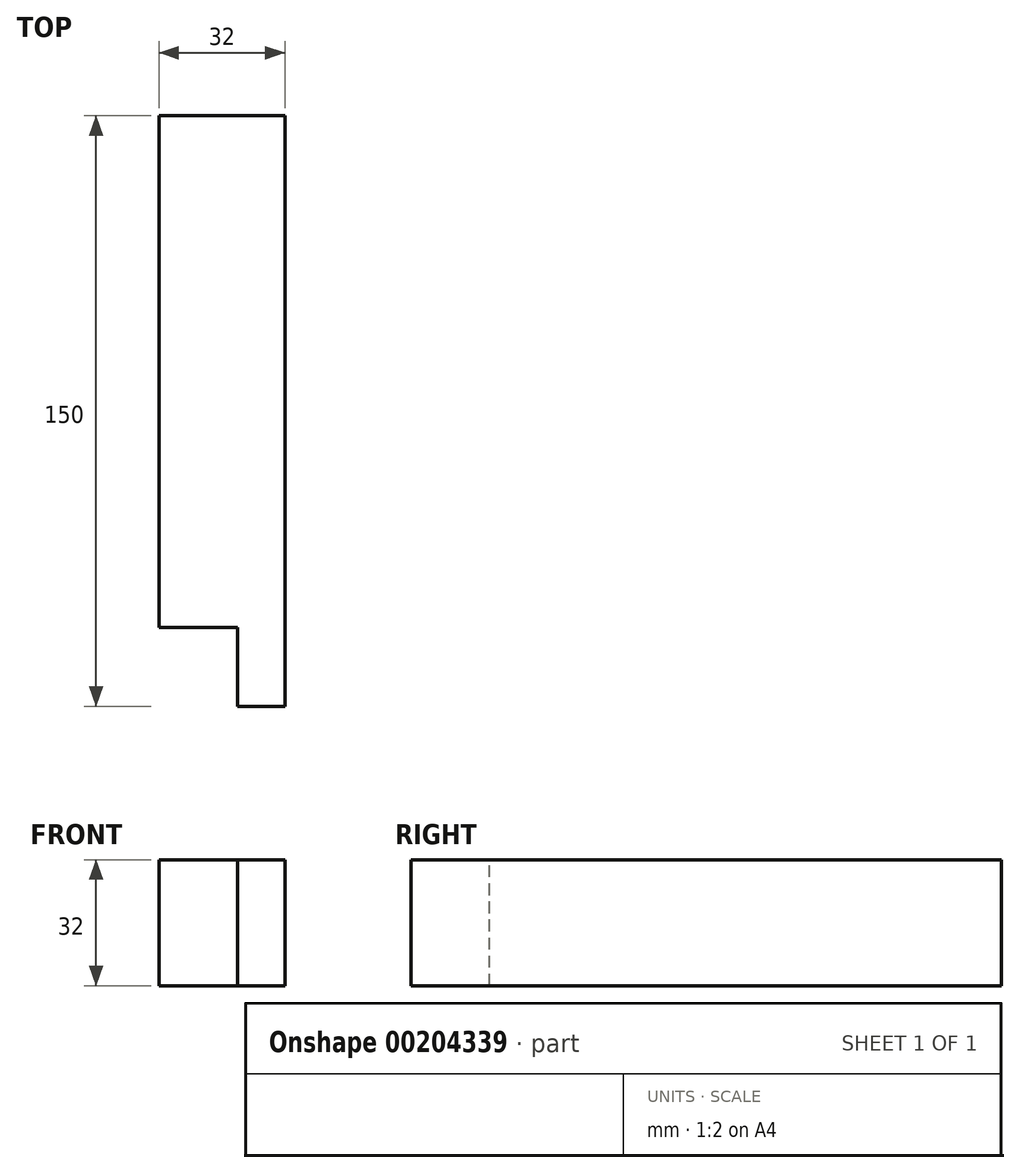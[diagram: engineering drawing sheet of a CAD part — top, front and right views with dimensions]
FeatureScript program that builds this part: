
annotation { "Feature Type Name" : "Feature", "Feature Type Description" : "" }
export const myFeature = defineFeature(function(context is Context, id is Id, definition is map)
    precondition{}
    {
        {
            var Q0;
            Q0=qCreatedBy(makeId("Front.planeOp"),FACE);
            var sketch = newSketch(context, id + "F0", { "sketchPlane" : qUnion([Q0])});
            skLineSegment(sketch, "E0.bottom", {"start": v(-16, -16) * mm, "end": v(16, -16) * mm});
            skLineSegment(sketch, "E0.top", {"start": v(-16, 16) * mm, "end": v(16, 16) * mm});
            skLineSegment(sketch, "E0.left", {"start": v(-16, -16) * mm, "end": v(-16, 16) * mm});
            skLineSegment(sketch, "E0.right", {"start": v(16, -16) * mm, "end": v(16, 16) * mm});
            skPoint(sketch, "E0.middle", {"position": v(0, 0) * mm});
            skSolve(sketch);
        }
        {
            var Q0;
            Q0 = qSketchRegion(id + "F0", true);
            extrude(context, id + "F1", {"entities" : qUnion([Q0]), "depth" : 150 * mm});
        }
        {
            var Q0;
            Q0=makeQuery(id+"F1.opExtrude","CAP_FACE",FACE,{"disambiguationData":[OSD([sQuery(id+"F0.wireOp",EDGE,"E0.bottom"),sQuery(id+"F0.wireOp",EDGE,"E0.top"),sQuery(id+"F0.wireOp",EDGE,"E0.left"),sQuery(id+"F0.wireOp",EDGE,"E0.right")])],"isStart":false});
            var sketch = newSketch(context, id + "F2", { "sketchPlane" : qUnion([Q0])});
            skLineSegment(sketch, "E1.bottom", {"start": v(-16, 16) * mm, "end": v(4, 16) * mm});
            skLineSegment(sketch, "E1.top", {"start": v(-16, -16) * mm, "end": v(4, -16) * mm});
            skLineSegment(sketch, "E1.left", {"start": v(-16, 16) * mm, "end": v(-16, -16) * mm});
            skLineSegment(sketch, "E1.right", {"start": v(4, 16) * mm, "end": v(4, -16) * mm});
            skSolve(sketch);
        }
        {
            var Q0;
            Q0 = qSketchRegion(id + "F2", true);
            extrude(context, id + "F3", {"entities" : qUnion([Q0]), "operationType" : NewBodyOperationType.REMOVE, "oppositeDirection" : true, "depth" : 20 * mm});
        }
    });
